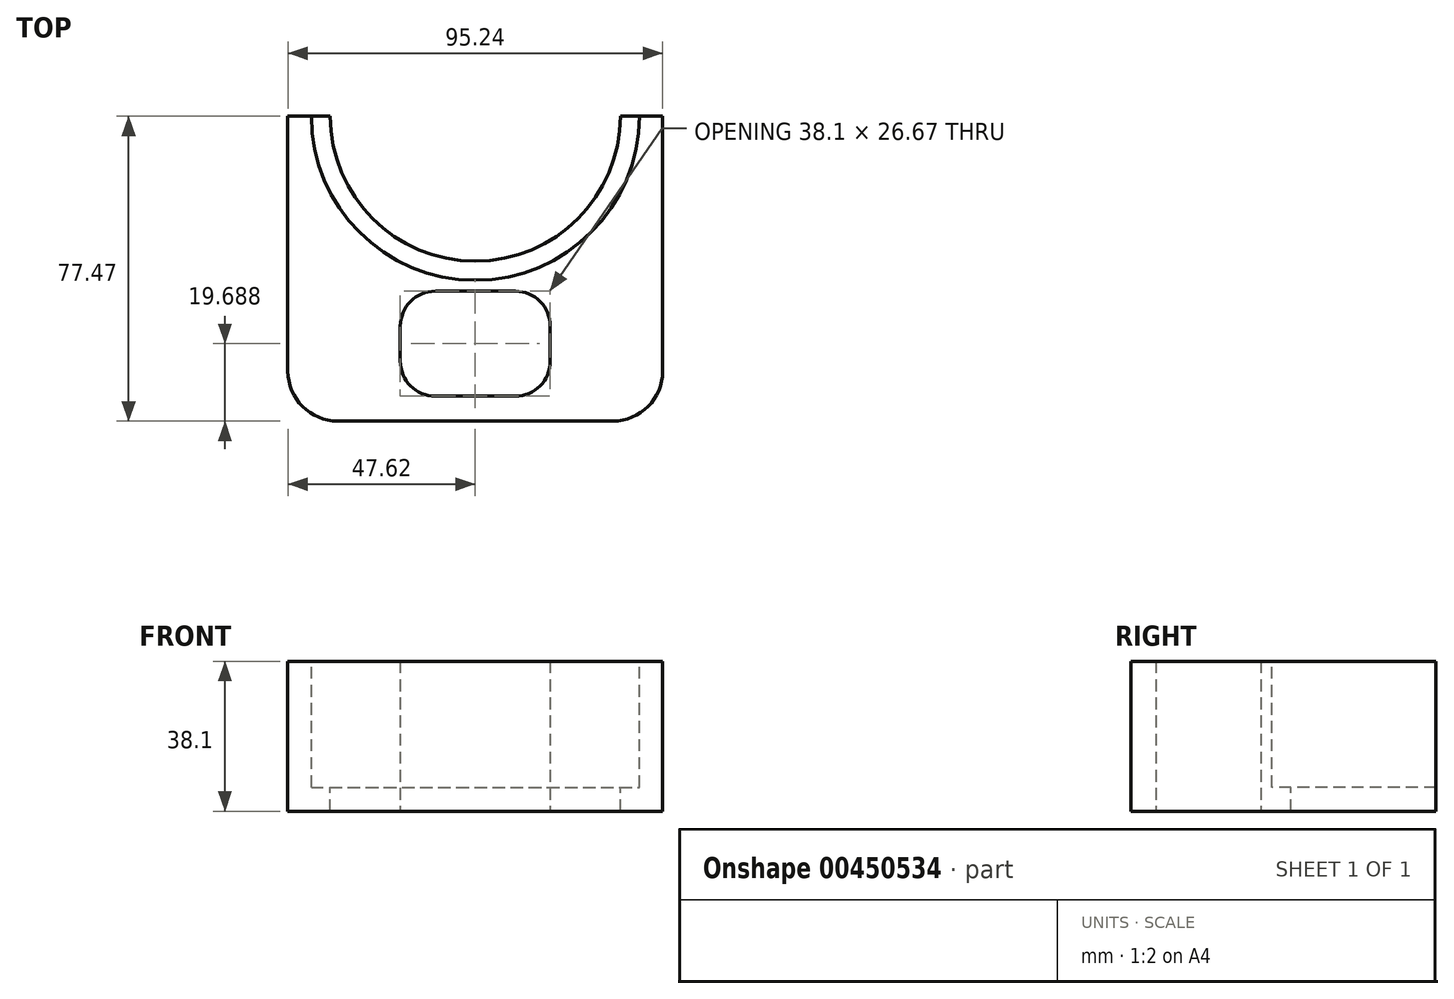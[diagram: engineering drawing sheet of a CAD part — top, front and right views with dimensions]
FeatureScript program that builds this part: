
annotation { "Feature Type Name" : "Feature", "Feature Type Description" : "" }
export const myFeature = defineFeature(function(context is Context, id is Id, definition is map)
    precondition{}
    {
        {
            var Q0;
            Q0=qCreatedBy(makeId("Top.planeOp"),FACE);
            var sketch = newSketch(context, id + "F0", { "sketchPlane" : qUnion([Q0])});
            skLineSegment(sketch, "E0.bottom", {"start": v(-47.63, 56) * mm, "end": v(47.62, 56) * mm});
            skLineSegment(sketch, "E0.top", {"start": v(-47.63, -21.47) * mm, "end": v(47.62, -21.47) * mm});
            skLineSegment(sketch, "E0.left", {"start": v(-47.63, 56) * mm, "end": v(-47.63, -21.47) * mm});
            skLineSegment(sketch, "E0.right", {"start": v(47.62, 56) * mm, "end": v(47.62, -21.47) * mm});
            skLineSegment(sketch, "E1.bottom", {"start": v(-19.05, 11.55) * mm, "end": v(19.05, 11.55) * mm});
            skLineSegment(sketch, "E1.top", {"start": v(-19.05, -15.12) * mm, "end": v(19.05, -15.12) * mm});
            skLineSegment(sketch, "E1.left", {"start": v(-19.05, 11.55) * mm, "end": v(-19.05, -15.12) * mm});
            skLineSegment(sketch, "E1.right", {"start": v(19.05, 11.55) * mm, "end": v(19.05, -15.12) * mm});
            skSolve(sketch);
        }
        {
            var Q0;
            Q0=makeQuery(id+"F0.imprint","IMPRINT",FACE,{"disambiguationData":[TD([[makeQuery(id+"F0.imprint","IMPRINT",EDGE,{"derivedFrom":sQuery(id+"F0.wireOp",EDGE,"E0.bottom")}),-1.0]])]});
            extrude(context, id + "F1", {"entities" : qUnion([Q0]), "depth" : 38.1 * mm});
        }
        {
            var Q0;
            Q0=makeQuery(id+"F1.opExtrude","SWEPT_EDGE",EDGE,{"disambiguationData":[OSD([sQuery(id+"F0.wireOp",EDGE,"E0.top"),sQuery(id+"F0.wireOp",EDGE,"E0.right")])]});
            var Q1;
            Q1=makeQuery(id+"F1.opExtrude","SWEPT_EDGE",EDGE,{"disambiguationData":[OSD([sQuery(id+"F0.wireOp",EDGE,"E0.top"),sQuery(id+"F0.wireOp",EDGE,"E0.left")])]});
            fillet(context, id + "F2", {"entities" : qUnion([Q0, Q1]), "radius" : 12.7 * mm, "tangentPropagation" : true, "allowEdgeOverflow" : false});
        }
        {
            var Q0;
            Q0=makeQuery(id+"F1.opExtrude","SWEPT_EDGE",EDGE,{"disambiguationData":[OSD([sQuery(id+"F0.wireOp",EDGE,"E1.top"),sQuery(id+"F0.wireOp",EDGE,"E1.right")])]});
            var Q1;
            Q1=makeQuery(id+"F1.opExtrude","SWEPT_EDGE",EDGE,{"disambiguationData":[OSD([sQuery(id+"F0.wireOp",EDGE,"E1.bottom"),sQuery(id+"F0.wireOp",EDGE,"E1.right")])]});
            var Q2;
            Q2=makeQuery(id+"F1.opExtrude","SWEPT_EDGE",EDGE,{"disambiguationData":[OSD([sQuery(id+"F0.wireOp",EDGE,"E1.bottom"),sQuery(id+"F0.wireOp",EDGE,"E1.left")])]});
            var Q3;
            Q3=makeQuery(id+"F1.opExtrude","SWEPT_EDGE",EDGE,{"disambiguationData":[OSD([sQuery(id+"F0.wireOp",EDGE,"E1.top"),sQuery(id+"F0.wireOp",EDGE,"E1.left")])]});
            fillet(context, id + "F3", {"entities" : qUnion([Q0, Q1, Q2, Q3]), "radius" : 8.9 * mm, "tangentPropagation" : true, "allowEdgeOverflow" : false});
        }
        {
            var Q0;
            Q0=makeQuery(id+"F1.opExtrude","CAP_FACE",FACE,{"disambiguationData":[OSD([sQuery(id+"F0.wireOp",EDGE,"E0.bottom"),sQuery(id+"F0.wireOp",EDGE,"E0.top"),sQuery(id+"F0.wireOp",EDGE,"E0.left"),sQuery(id+"F0.wireOp",EDGE,"E0.right"),sQuery(id+"F0.wireOp",EDGE,"E1.bottom"),sQuery(id+"F0.wireOp",EDGE,"E1.top"),sQuery(id+"F0.wireOp",EDGE,"E1.left"),sQuery(id+"F0.wireOp",EDGE,"E1.right")])],"isStart":false});
            var sketch = newSketch(context, id + "F4", { "sketchPlane" : qUnion([Q0])});
            skCircle(sketch, "E2", {"center": v(0, 56) * mm, "radius": 41.66 * mm});
            skSolve(sketch);
        }
        {
            var Q0;
            {var subQ0=sQuery(id+"F4.wireOp",EDGE,"E2");var subQ1=makeQuery(id+"F1.opExtrude","CAP_EDGE",EDGE,{"disambiguationData":[OSD([sQuery(id+"F0.wireOp",EDGE,"E0.bottom")])],"isStart":false});var subQ2=makeQuery(id+"F4.imprint","INTERSECT",VERTEX,{"disambiguationData":[OD(0.0)],"derivedFrom":[subQ1,subQ0]});Q0=makeQuery(id+"F4.imprint","IMPRINT",FACE,{"disambiguationData":[TD([[makeQuery(id+"F4.imprint","IMPRINT",EDGE,{"disambiguationData":[TD([[subQ2,-1.0]])],"derivedFrom":subQ0}),1.0]])]});}
            extrude(context, id + "F5", {"entities" : qUnion([Q0]), "operationType" : NewBodyOperationType.REMOVE, "oppositeDirection" : true, "depth" : 32 * mm});
        }
        {
            var Q0;
            Q0=makeQuery(id+"F5.boolean.opBoolean","COPY",FACE,{"derivedFrom":makeQuery(id+"F5.opExtrude","CAP_FACE",FACE,{"disambiguationData":[OSD([sQuery(id+"F0.wireOp",EDGE,"E0.bottom"),sQuery(id+"F4.wireOp",EDGE,"E2")])],"isStart":false})});
            var sketch = newSketch(context, id + "F6", { "sketchPlane" : qUnion([Q0])});
            skCircle(sketch, "E3", {"center": v(0, 56) * mm, "radius": 36.83 * mm});
            skSolve(sketch);
        }
        {
            var Q0;
            {var subQ0=sQuery(id+"F6.wireOp",EDGE,"E3");var subQ1=makeQuery(id+"F5.boolean.opBoolean","COPY",EDGE,{"derivedFrom":makeQuery(id+"F5.opExtrude","CAP_EDGE",EDGE,{"disambiguationData":[OSD([sQuery(id+"F0.wireOp",EDGE,"E0.bottom")])],"isStart":false})});var subQ2=makeQuery(id+"F6.imprint","INTERSECT",VERTEX,{"disambiguationData":[OD(0.0)],"derivedFrom":[subQ1,subQ0]});Q0=makeQuery(id+"F6.imprint","IMPRINT",FACE,{"disambiguationData":[TD([[makeQuery(id+"F6.imprint","IMPRINT",EDGE,{"disambiguationData":[TD([[subQ2,-1.0]])],"derivedFrom":subQ0}),1.0]])]});}
            extrude(context, id + "F7", {"entities" : qUnion([Q0]), "operationType" : NewBodyOperationType.REMOVE, "oppositeDirection" : true, "depth" : 25.4 * mm});
        }
    });
